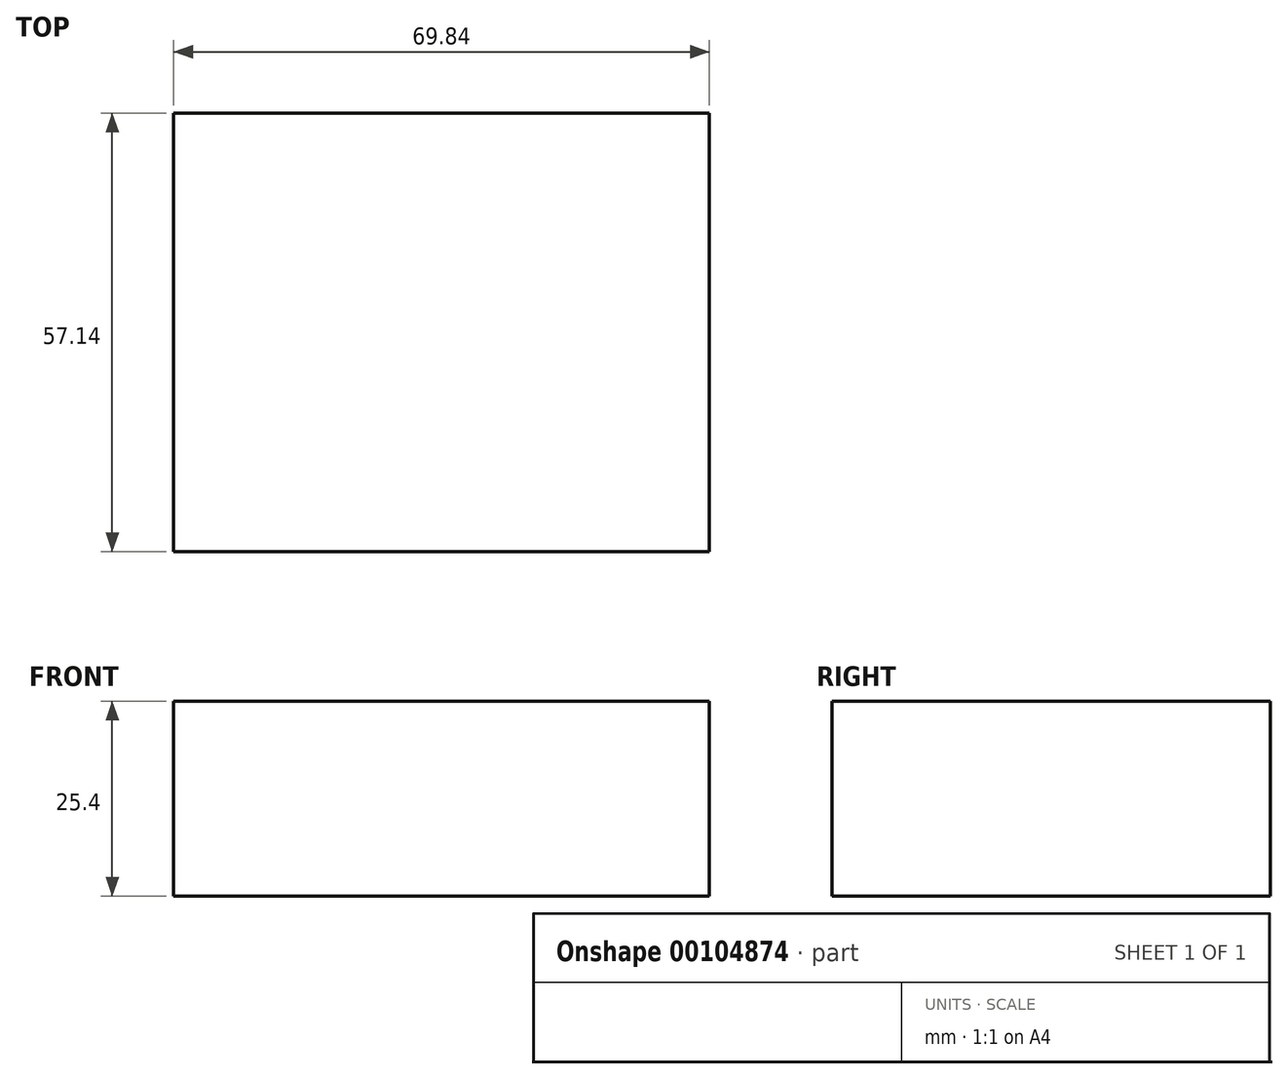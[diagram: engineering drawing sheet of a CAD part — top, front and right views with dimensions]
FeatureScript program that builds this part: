
annotation { "Feature Type Name" : "Feature", "Feature Type Description" : "" }
export const myFeature = defineFeature(function(context is Context, id is Id, definition is map)
    precondition{}
    {
        {
            var Q0;
            Q0=qCreatedBy(makeId("Top.planeOp"),FACE);
            var sketch = newSketch(context, id + "F0", { "sketchPlane" : qUnion([Q0])});
            skLineSegment(sketch, "E0.bottom", {"start": v(-34.92, 28.58) * mm, "end": v(34.93, 28.58) * mm});
            skLineSegment(sketch, "E0.top", {"start": v(-34.93, -28.57) * mm, "end": v(34.92, -28.57) * mm});
            skLineSegment(sketch, "E0.left", {"start": v(-34.92, 28.57) * mm, "end": v(-34.93, -28.57) * mm});
            skLineSegment(sketch, "E0.right", {"start": v(34.93, 28.57) * mm, "end": v(34.92, -28.57) * mm});
            skPoint(sketch, "E0.middle", {"position": v(0, 0) * mm});
            skSolve(sketch);
        }
        {
            var Q0;
            Q0=makeQuery(id+"F0.imprint","IMPRINT",FACE,{"disambiguationData":[TD([[makeQuery(id+"F0.imprint","IMPRINT",EDGE,{"derivedFrom":sQuery(id+"F0.wireOp",EDGE,"E0.bottom")}),-1.0]])]});
            extrude(context, id + "F1", {"entities" : qUnion([Q0]), "depth" : 25.4 * mm});
        }
    });
